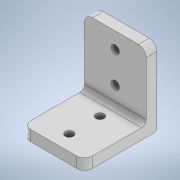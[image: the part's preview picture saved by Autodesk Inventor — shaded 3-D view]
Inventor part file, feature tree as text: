
AUTODESK INVENTOR PART (.ipt)
format: ipt  version: 2022 (Build 260153000, 153)  size: 144,384 bytes
history: native  units: mm
features: sketch x4, extrude x2, hole x2, fillet x1
ambient origin geometry x8: Origin, YZ Plane, XZ Plane, XY Plane, X Axis, Y Axis, Z Axis, Center Point
bodies: Solid1 (feature_tree)
feature tree (9):
  extrude  "Extrusion1"  Depth=40.0mm
  sketch  "Sketch2"  dims[d2=7.0mm d3=0.0mm d4=20.0mm d5=10.0mm]
  extrude  "Extrusion2"  Depth=10.0mm
  fillet  "Fillet2"  Radius=10.0mm
  hole  "Hole4"  [1 undecoded]
  hole  "Hole5"  [1 undecoded]
  sketch  "Sketch1"  dims[d0=40.0mm d1=40.0mm]
  sketch  "Sketch3"  dims[d14=50.0mm d15=40.0mm]
  sketch  "Sketch4"  dims[d16=7.0mm d17=0.0mm d19=3.0mm d20=5.0mm d21=2.0mm d22=20.0mm d23=12.5mm d38=5.4mm d39=6.0mm d40=4.0mm d41=2.0mm d42=90.0deg d43=8.0mm d44=20.594885mm d45=5.4mm d46=6.0mm d47=4.0mm d48=2.0mm d49=90.0deg d50=8.0mm d51=20.594885mm]
note: 2 required parameter values undecoded (feature->parameter linkage not recoverable at this tier; creation-order binding heuristic only, values carry confidence <= 0.55)
